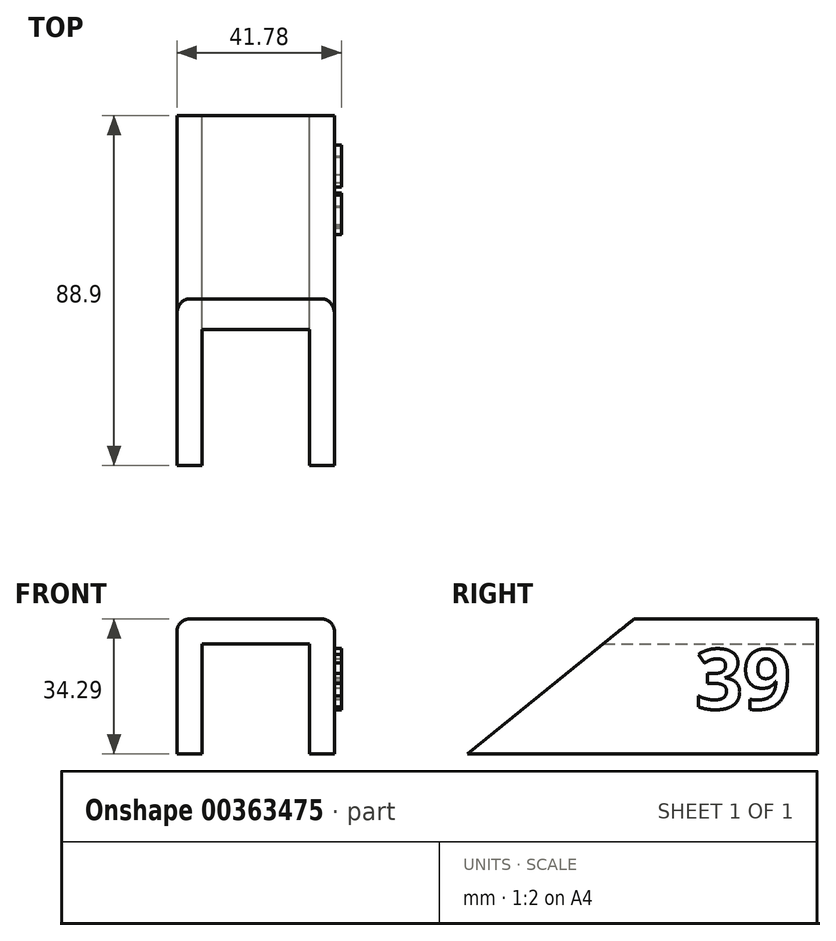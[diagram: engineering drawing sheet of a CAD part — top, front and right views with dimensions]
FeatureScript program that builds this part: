
annotation { "Feature Type Name" : "Feature", "Feature Type Description" : "" }
export const myFeature = defineFeature(function(context is Context, id is Id, definition is map)
    precondition{}
    {
        {
            var Q0;
            Q0=qCreatedBy(makeId("Front.planeOp"),FACE);
            var sketch = newSketch(context, id + "F0", { "sketchPlane" : qUnion([Q0])});
            skLineSegment(sketch, "E0.bottom", {"start": v(0, 0) * mm, "end": v(6.35, 0) * mm});
            skLineSegment(sketch, "E0.top", {"start": v(0, 34.3) * mm, "end": v(40, 34.3) * mm});
            skLineSegment(sketch, "E0.left", {"start": v(0, 0) * mm, "end": v(0, 34.3) * mm});
            skLineSegment(sketch, "E0.right", {"start": v(40, 0) * mm, "end": v(40, 34.3) * mm});
            skLineSegment(sketch, "E1", {"start": v(6.35, 0) * mm, "end": v(6.35, 27.94) * mm});
            skLineSegment(sketch, "E2", {"start": v(6.35, 27.94) * mm, "end": v(33.65, 27.94) * mm});
            skLineSegment(sketch, "E3", {"start": v(33.65, 27.94) * mm, "end": v(33.65, 0) * mm});
            skLineSegment(sketch, "E4.trimOffspring", {"start": v(33.65, 0) * mm, "end": v(40, 0) * mm});
            skSolve(sketch);
        }
        {
            var Q0;
            Q0=makeQuery(id+"F0.imprint","IMPRINT",FACE,{"disambiguationData":[TD([[makeQuery(id+"F0.imprint","IMPRINT",EDGE,{"derivedFrom":sQuery(id+"F0.wireOp",EDGE,"E0.bottom")}),1.0]])]});
            extrude(context, id + "F1", {"entities" : qUnion([Q0]), "depth" : 50.8 * mm, "hasSecondDirection" : true, "secondDirectionOppositeDirection" : true, "secondDirectionDepth" : 38.1 * mm});
        }
        {
            var Q0;
            Q0=makeQuery(id+"F1.opExtrude","SWEPT_FACE",FACE,{"disambiguationData":[OSD([sQuery(id+"F0.wireOp",EDGE,"E0.right")])]});
            var sketch = newSketch(context, id + "F2", { "sketchPlane" : qUnion([Q0])});
            skLineSegment(sketch, "E5", {"start": v(-8.46, 34.3) * mm, "end": v(-50.8, 0) * mm});
            skLineSegment(sketch, "E6", {"start": v(-50.8, 0) * mm, "end": v(-50.8, 34.3) * mm});
            skLineSegment(sketch, "E7", {"start": v(-50.8, 34.3) * mm, "end": v(-8.46, 34.3) * mm});
            skSolve(sketch);
        }
        {
            var Q0;
            Q0=makeQuery(id+"F2.imprint","IMPRINT",FACE,{"disambiguationData":[TD([[makeQuery(id+"F2.imprint","IMPRINT",EDGE,{"derivedFrom":sQuery(id+"F2.wireOp",EDGE,"E5")}),-1.0]])]});
            extrude(context, id + "F3", {"entities" : qUnion([Q0]), "operationType" : NewBodyOperationType.REMOVE, "endBound" : BoundingType.THROUGH_ALL, "oppositeDirection" : true, "depth" : 25.4 * mm});
        }
        {
            var Q0;
            Q0=makeQuery(id+"F1.opExtrude","SWEPT_FACE",FACE,{"disambiguationData":[OSD([sQuery(id+"F0.wireOp",EDGE,"E0.right")])]});
            var sketch = newSketch(context, id + "F4", { "sketchPlane" : qUnion([Q0])});
            skText(sketch, "E8", { "text": "39\n", "fontName": "OpenSans-Bold.ttf"});
            const initialGuessF4  = {"E8": [0.0071, 0.0114, 1, 0, 0.01527]};
            skSetInitialGuess(sketch, initialGuessF4);
            skSolve(sketch);
        }
        {
            var Q0;
            Q0 = qSketchRegion(id + "F4", true);
            extrude(context, id + "F5", {"entities" : qUnion([Q0]), "operationType" : NewBodyOperationType.ADD, "depth" : 1.78 * mm});
        }
        {
            var Q0;
            Q0=makeQuery(id+"F1.opExtrude","SWEPT_EDGE",EDGE,{"disambiguationData":[OSD([sQuery(id+"F0.wireOp",EDGE,"E0.top"),sQuery(id+"F0.wireOp",EDGE,"E0.right")])]});
            var Q1;
            Q1=makeQuery(id+"F1.opExtrude","SWEPT_EDGE",EDGE,{"disambiguationData":[OSD([sQuery(id+"F0.wireOp",EDGE,"E0.top"),sQuery(id+"F0.wireOp",EDGE,"E0.left")])]});
            fillet(context, id + "F6", {"entities" : qUnion([Q0, Q1]), "radius" : 3.17 * mm, "tangentPropagation" : true, "allowEdgeOverflow" : false});
        }
    });
